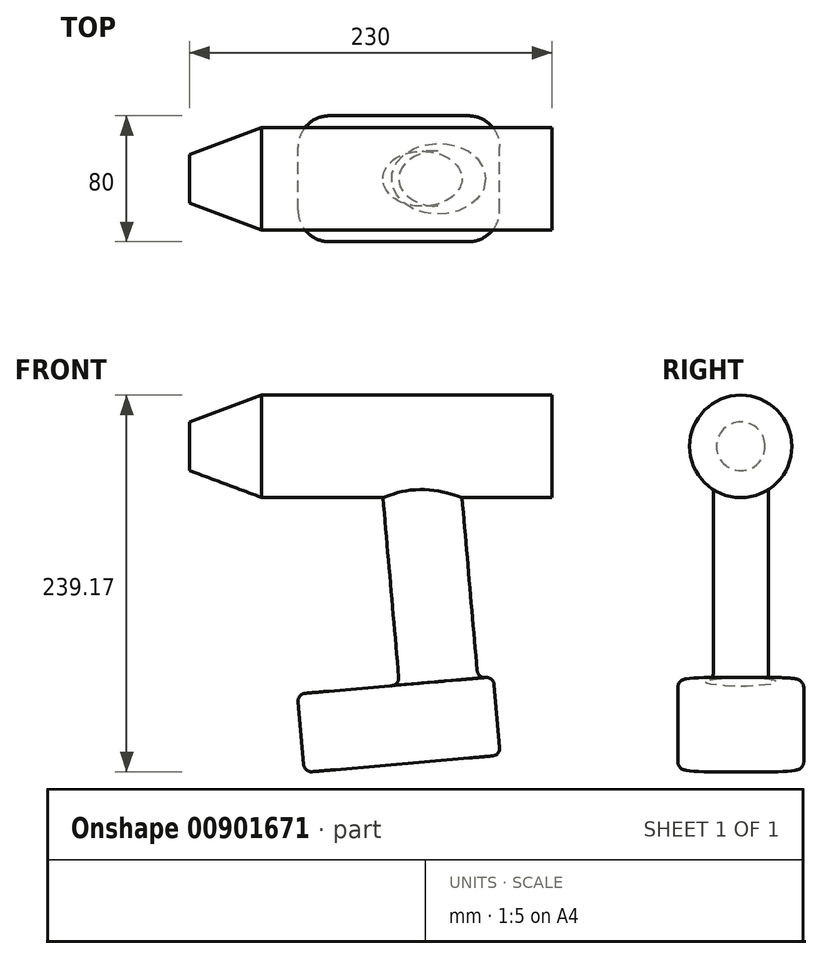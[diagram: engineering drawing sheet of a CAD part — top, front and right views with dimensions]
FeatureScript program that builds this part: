
annotation { "Feature Type Name" : "Feature", "Feature Type Description" : "" }
export const myFeature = defineFeature(function(context is Context, id is Id, definition is map)
    precondition{}
    {
        {
            var Q0;
            Q0=qCreatedBy(makeId("Right.planeOp"),FACE);
            var sketch = newSketch(context, id + "F0", { "sketchPlane" : qUnion([Q0])});
            skCircle(sketch, "E0", {"center": v(0, 0) * mm, "radius": 32.5 * mm});
            skSolve(sketch);
        }
        {
            var Q0;
            Q0=makeQuery(id+"F0.imprint","IMPRINT",FACE,{"disambiguationData":[TD([[makeQuery(id+"F0.imprint","IMPRINT",EDGE,{"derivedFrom":sQuery(id+"F0.wireOp",EDGE,"E0")}),1.0]])]});
            extrude(context, id + "F1", {"entities" : qUnion([Q0]), "depth" : 85 * mm, "offsetDistance" : 25.4 * mm, "hasSecondDirection" : true, "secondDirectionOppositeDirection" : true, "secondDirectionDepth" : 145 * mm});
        }
        {
            var Q0;
            Q0=qCreatedBy(makeId("Top.planeOp"),FACE);
            var sketch = newSketch(context, id + "F2", { "sketchPlane" : qUnion([Q0])});
            skLineSegment(sketch, "E1", {"start": v(0, 49.9) * mm, "end": v(0, -54.3) * mm, "construction": true});
            skSolve(sketch);
        }
        {
            var Q0;
            Q0=sQuery(id+"F2.wireOp",EDGE,"E1");
            var Q1;
            Q1=qCreatedBy(makeId("Top.planeOp"),FACE);
            cPlane(context, id + "F3", {"entities" : qUnion([Q0, Q1]), "cplaneType" : CPlaneType.LINE_ANGLE, "offset" : 25.4 * mm, "angle" : 5 * degree, "width" : 152.4 * mm, "height" : 152.4 * mm});
        }
        {
            var Q0;
            Q0=qCreatedBy(id+"F3.planeOp",FACE);
            var sketch = newSketch(context, id + "F4", { "sketchPlane" : qUnion([Q0])});
            skEllipse(sketch, "E2", {"center": v(0, 0) * mm, "majorRadius": 25 * mm, "minorRadius": 17.5 * mm, "majorAxis": v(1, 0)});
            skSolve(sketch);
        }
        {
            var Q0;
            Q0=qSketchRegion(id+"F4",true);
            extrude(context, id + "F5", {"entities" : qUnion([Q0]), "operationType" : NewBodyOperationType.ADD, "depth" : 150 * mm, "offsetDistance" : 25.4 * mm});
        }
        {
            var Q0;
            Q0=makeQuery(id+"F5.opExtrude","CAP_FACE",FACE,{"disambiguationData":[OSD([sQuery(id+"F4.wireOp",EDGE,"E2")])],"isStart":false});
            cPlane(context, id + "F6", {"entities" : qUnion([Q0]), "cplaneType" : CPlaneType.OFFSET, "offset" : 0 * mm, "oppositeDirection" : true, "width" : 152.4 * mm, "height" : 152.4 * mm});
        }
        {
            var Q0;
            Q0=qCreatedBy(id+"F6.planeOp",FACE);
            var sketch = newSketch(context, id + "F7", { "sketchPlane" : qUnion([Q0])});
            skPoint(sketch, "E3", {"position": v(0, 0) * mm});
            skLineSegment(sketch, "E4.bottom", {"start": v(35, 40) * mm, "end": v(-90, 40) * mm});
            skLineSegment(sketch, "E4.top", {"start": v(35, -40) * mm, "end": v(-90, -40) * mm});
            skLineSegment(sketch, "E4.left", {"start": v(35, 40) * mm, "end": v(35, -40) * mm});
            skLineSegment(sketch, "E4.right", {"start": v(-90, 40) * mm, "end": v(-90, -40) * mm});
            skLineSegment(sketch, "E5", {"start": v(0, 97.32) * mm, "end": v(0, -100.26) * mm, "construction": true});
            skLineSegment(sketch, "E6", {"start": v(103.8, 0) * mm, "end": v(-154.14, 0) * mm, "construction": true});
            skSolve(sketch);
        }
        {
            var Q0;
            Q0=makeQuery(id+"F7.imprint","IMPRINT",FACE,{"disambiguationData":[TD([[makeQuery(id+"F7.imprint","IMPRINT",EDGE,{"derivedFrom":sQuery(id+"F7.wireOp",EDGE,"E4.bottom")}),1.0]])]});
            extrude(context, id + "F8", {"entities" : qUnion([Q0]), "operationType" : NewBodyOperationType.ADD, "depth" : 50 * mm, "offsetDistance" : 25.4 * mm});
        }
        {
            var Q0;
            Q0=qCreatedBy(makeId("Front.planeOp"),FACE);
            var sketch = newSketch(context, id + "F9", { "sketchPlane" : qUnion([Q0])});
            skLineSegment(sketch, "E7", {"start": v(-145, 15.47) * mm, "end": v(-99.3, 32.5) * mm});
            skLineSegment(sketch, "E8", {"start": v(-145, 15.47) * mm, "end": v(-145, 32.5) * mm});
            skLineSegment(sketch, "E9", {"start": v(-99.3, 32.5) * mm, "end": v(-145, 32.5) * mm});
            skLineSegment(sketch, "E10", {"start": v(-216.27, 0) * mm, "end": v(81.4, 0) * mm, "construction": true});
            skSolve(sketch);
        }
        {
            var Q0;
            Q0=qSketchRegion(id+"F9",true);
            var Q1;
            Q1=sQuery(id+"F9.wireOp",EDGE,"E10");
            revolve(context, id + "F10", {"operationType" : NewBodyOperationType.REMOVE, "surfaceOperationType" : NewSurfaceOperationType.NEW, "entities" : qUnion([Q0]), "axis" : qUnion([Q1]), "revolveType" : RevolveType.FULL, "oppositeDirection" : true});
        }
        {
            var Q0;
            Q0=makeQuery(id+"F8.opExtrude","SWEPT_EDGE",EDGE,{"disambiguationData":[OSD([sQuery(id+"F7.wireOp",EDGE,"E4.top"),sQuery(id+"F7.wireOp",EDGE,"E4.right")])]});
            var Q1;
            Q1=makeQuery(id+"F8.opExtrude","SWEPT_EDGE",EDGE,{"disambiguationData":[OSD([sQuery(id+"F7.wireOp",EDGE,"E4.bottom"),sQuery(id+"F7.wireOp",EDGE,"E4.right")])]});
            var Q2;
            Q2=makeQuery(id+"F8.opExtrude","SWEPT_EDGE",EDGE,{"disambiguationData":[OSD([sQuery(id+"F7.wireOp",EDGE,"E4.bottom"),sQuery(id+"F7.wireOp",EDGE,"E4.left")])]});
            var Q3;
            Q3=makeQuery(id+"F8.opExtrude","SWEPT_EDGE",EDGE,{"disambiguationData":[OSD([sQuery(id+"F7.wireOp",EDGE,"E4.top"),sQuery(id+"F7.wireOp",EDGE,"E4.left")])]});
            fillet(context, id + "F11", {"entities" : qUnion([Q0, Q1, Q2, Q3]), "radius" : 20 * mm, "tangentPropagation" : true, "allowEdgeOverflow" : false});
        }
        {
            var Q0;
            Q0=makeQuery(id+"F5.opExtrude","CAP_EDGE",EDGE,{"disambiguationData":[OSD([sQuery(id+"F4.wireOp",EDGE,"E2")])],"isStart":false});
            var Q1;
            Q1=makeQuery(id+"F8.opExtrude","CAP_FACE",FACE,{"disambiguationData":[OSD([sQuery(id+"F7.wireOp",EDGE,"E4.bottom"),sQuery(id+"F7.wireOp",EDGE,"E4.top"),sQuery(id+"F7.wireOp",EDGE,"E4.left"),sQuery(id+"F7.wireOp",EDGE,"E4.right")])],"isStart":true});
            var Q2;
            Q2=makeQuery(id+"F8.opExtrude","CAP_FACE",FACE,{"disambiguationData":[OSD([sQuery(id+"F7.wireOp",EDGE,"E4.bottom"),sQuery(id+"F7.wireOp",EDGE,"E4.top"),sQuery(id+"F7.wireOp",EDGE,"E4.left"),sQuery(id+"F7.wireOp",EDGE,"E4.right")])],"isStart":false});
            fillet(context, id + "F12", {"entities" : qUnion([Q0, Q1, Q2]), "radius" : 5 * mm, "tangentPropagation" : true, "allowEdgeOverflow" : false});
        }
    });
